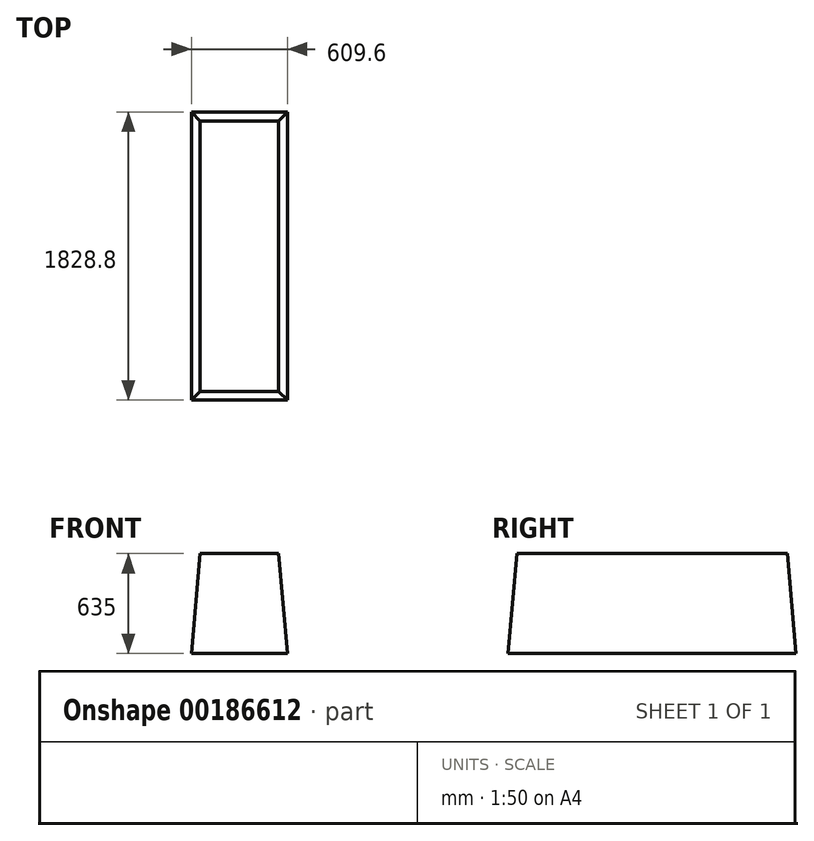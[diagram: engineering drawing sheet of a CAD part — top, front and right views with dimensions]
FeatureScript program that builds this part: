
annotation { "Feature Type Name" : "Feature", "Feature Type Description" : "" }
export const myFeature = defineFeature(function(context is Context, id is Id, definition is map)
    precondition{}
    {
        {
            var Q0;
            Q0=qCreatedBy(makeId("Top.planeOp"),FACE);
            var sketch = newSketch(context, id + "F0", { "sketchPlane" : qUnion([Q0])});
            skLineSegment(sketch, "E0.bottom", {"start": v(304.8, -914.4) * mm, "end": v(-304.8, -914.4) * mm});
            skLineSegment(sketch, "E0.top", {"start": v(304.8, 914.4) * mm, "end": v(-304.8, 914.4) * mm});
            skLineSegment(sketch, "E0.left", {"start": v(304.8, -914.4) * mm, "end": v(304.8, 914.4) * mm});
            skLineSegment(sketch, "E0.right", {"start": v(-304.8, -914.4) * mm, "end": v(-304.8, 914.4) * mm});
            skPoint(sketch, "E0.middle", {"position": v(0, 0) * mm});
            skSolve(sketch);
        }
        {
            var Q0;
            Q0=makeQuery(id+"F0.imprint","IMPRINT",FACE,{"disambiguationData":[TD([[makeQuery(id+"F0.imprint","IMPRINT",EDGE,{"derivedFrom":sQuery(id+"F0.wireOp",EDGE,"E0.bottom")}),-1.0]])]});
            extrude(context, id + "F1", {"entities" : qUnion([Q0]), "depth" : 635 * mm, "hasDraft" : true, "draftAngle" : 5 * degree, "draftPullDirection" : true});
        }
    });
